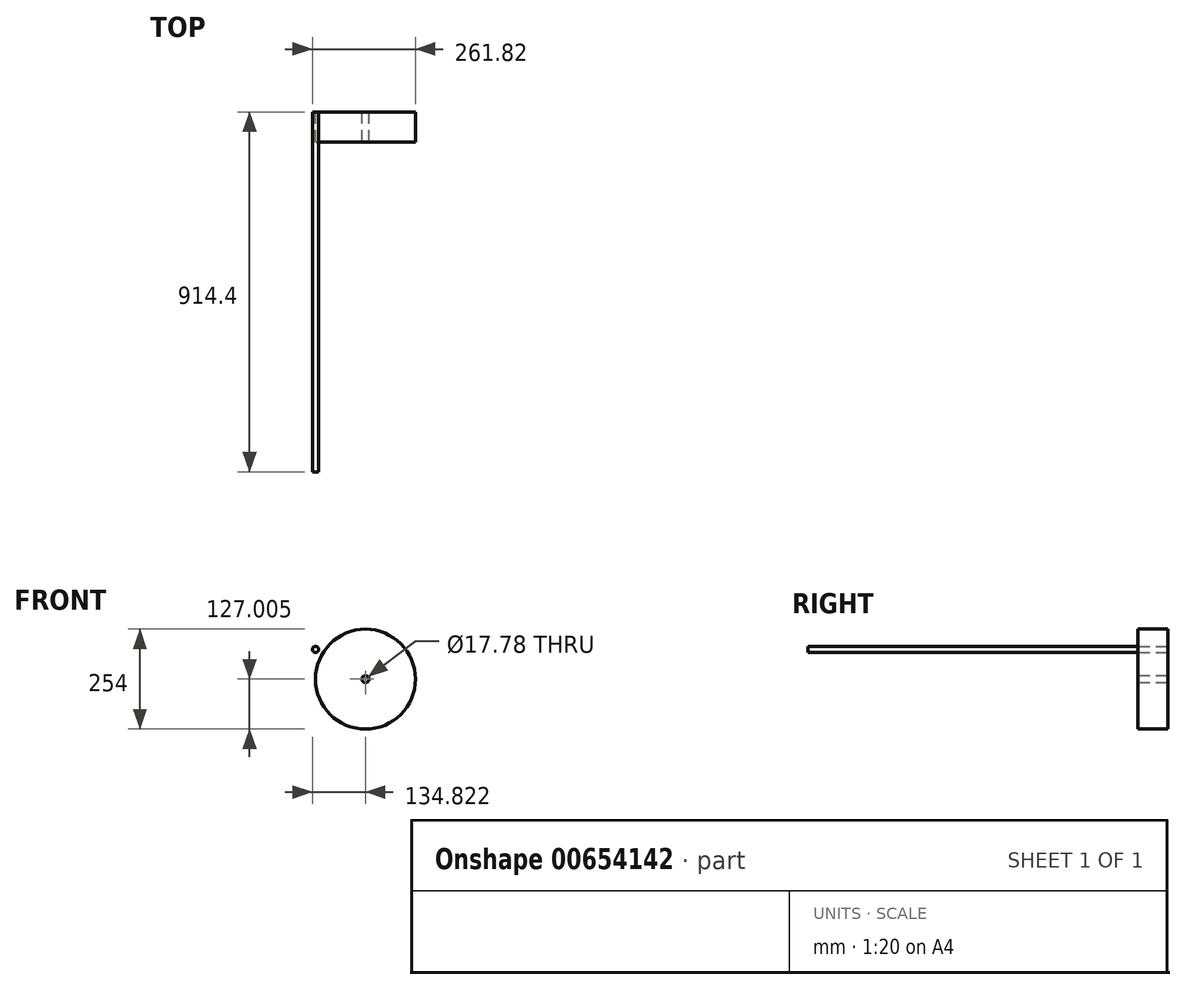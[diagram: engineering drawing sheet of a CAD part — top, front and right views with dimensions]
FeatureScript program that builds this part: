
annotation { "Feature Type Name" : "Feature", "Feature Type Description" : "" }
export const myFeature = defineFeature(function(context is Context, id is Id, definition is map)
    precondition{}
    {
        {
            var Q0;
            Q0=qCreatedBy(makeId("Front.planeOp"),FACE);
            var sketch = newSketch(context, id + "F0", { "sketchPlane" : qUnion([Q0])});
            skCircle(sketch, "E0", {"center": v(-27.2, 32.8) * mm, "radius": 7.94 * mm});
            skCircle(sketch, "E1", {"center": v(99.68, -43) * mm, "radius": 127 * mm});
            skCircle(sketch, "E2", {"center": v(99.68, -43) * mm, "radius": 8.9 * mm});
            skSolve(sketch);
        }
        {
            var Q0;
            Q0=makeQuery(id+"F0.imprint","IMPRINT",FACE,{"disambiguationData":[TD([[makeQuery(id+"F0.imprint","IMPRINT",EDGE,{"derivedFrom":sQuery(id+"F0.wireOp",EDGE,"E0")}),1.0]])]});
            extrude(context, id + "F1", {"entities" : qUnion([Q0]), "depth" : 914.4 * mm, "offsetDistance" : 25.4 * mm});
        }
        {
            var Q0;
            Q0=makeQuery(id+"F0.imprint","IMPRINT",FACE,{"disambiguationData":[TD([[makeQuery(id+"F0.imprint","IMPRINT",EDGE,{"derivedFrom":sQuery(id+"F0.wireOp",EDGE,"E1")}),1.0]])]});
            extrude(context, id + "F2", {"entities" : qUnion([Q0]), "depth" : 76.2 * mm, "offsetDistance" : 25.4 * mm});
        }
    });
